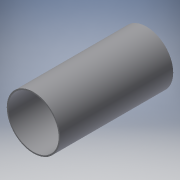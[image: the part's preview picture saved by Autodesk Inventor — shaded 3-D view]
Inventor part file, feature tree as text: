
AUTODESK INVENTOR PART (.ipt)
format: ipt  version: 2019 (Build 230136000, 136)  size: 97,280 bytes
history: native  units: mm
features: other x4, extrude x1, sketch x1, reference x1
ambient origin geometry x8: Origin, YZ Plane, XZ Plane, XY Plane, X Axis, Y Axis, Z Axis, Center Point
bodies: Body1 (feature_tree)
feature tree (7):
  other  "Твердое тело1"
  extrude  "Выдавливание1"  Depth=170.0mm TaperAngle=0.0deg
  sketch  "Эскиз1"
  reference  "Ссылка1"
  other  "<userpath>\Documents\GitHub\Tesla_coil_V1\3dModels\TeslaCoil.iam"
  other  "TeslaCoil.iam"
  other  "Cap:1"
